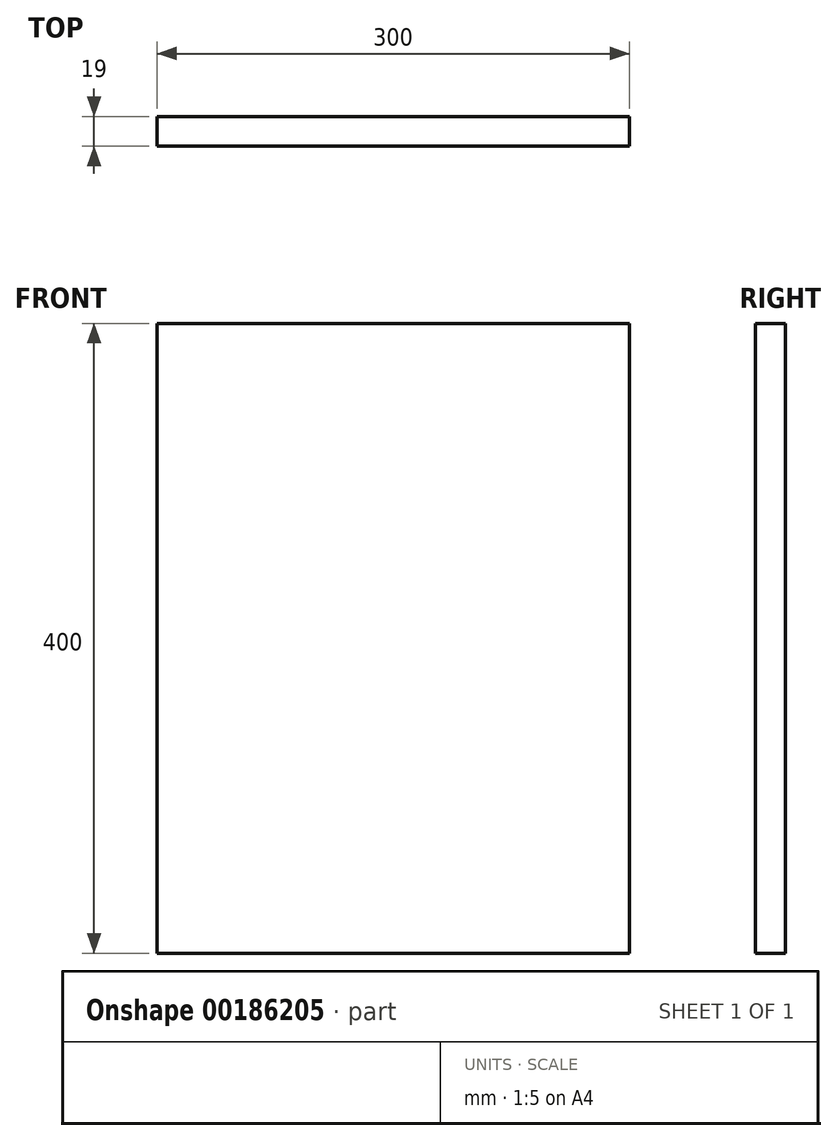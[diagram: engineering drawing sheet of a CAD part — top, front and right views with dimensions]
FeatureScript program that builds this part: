
annotation { "Feature Type Name" : "Feature", "Feature Type Description" : "" }
export const myFeature = defineFeature(function(context is Context, id is Id, definition is map)
    precondition{}
    {
        {
            var Q0;
            Q0=qCreatedBy(makeId("Front.planeOp"),FACE);
            var sketch = newSketch(context, id + "F0", { "sketchPlane" : qUnion([Q0])});
            skLineSegment(sketch, "E0.bottom", {"start": v(-99.35, 157.4) * mm, "end": v(200.65, 157.4) * mm});
            skLineSegment(sketch, "E0.top", {"start": v(-99.35, -242.6) * mm, "end": v(200.65, -242.6) * mm});
            skLineSegment(sketch, "E0.left", {"start": v(-99.35, 157.4) * mm, "end": v(-99.35, -242.6) * mm});
            skLineSegment(sketch, "E0.right", {"start": v(200.65, 157.4) * mm, "end": v(200.65, -242.6) * mm});
            skSolve(sketch);
        }
        {
            var Q0;
            Q0 = qSketchRegion(id + "F0", true);
            extrude(context, id + "F1", {"entities" : qUnion([Q0]), "depth" : 19 * mm});
        }
    });
